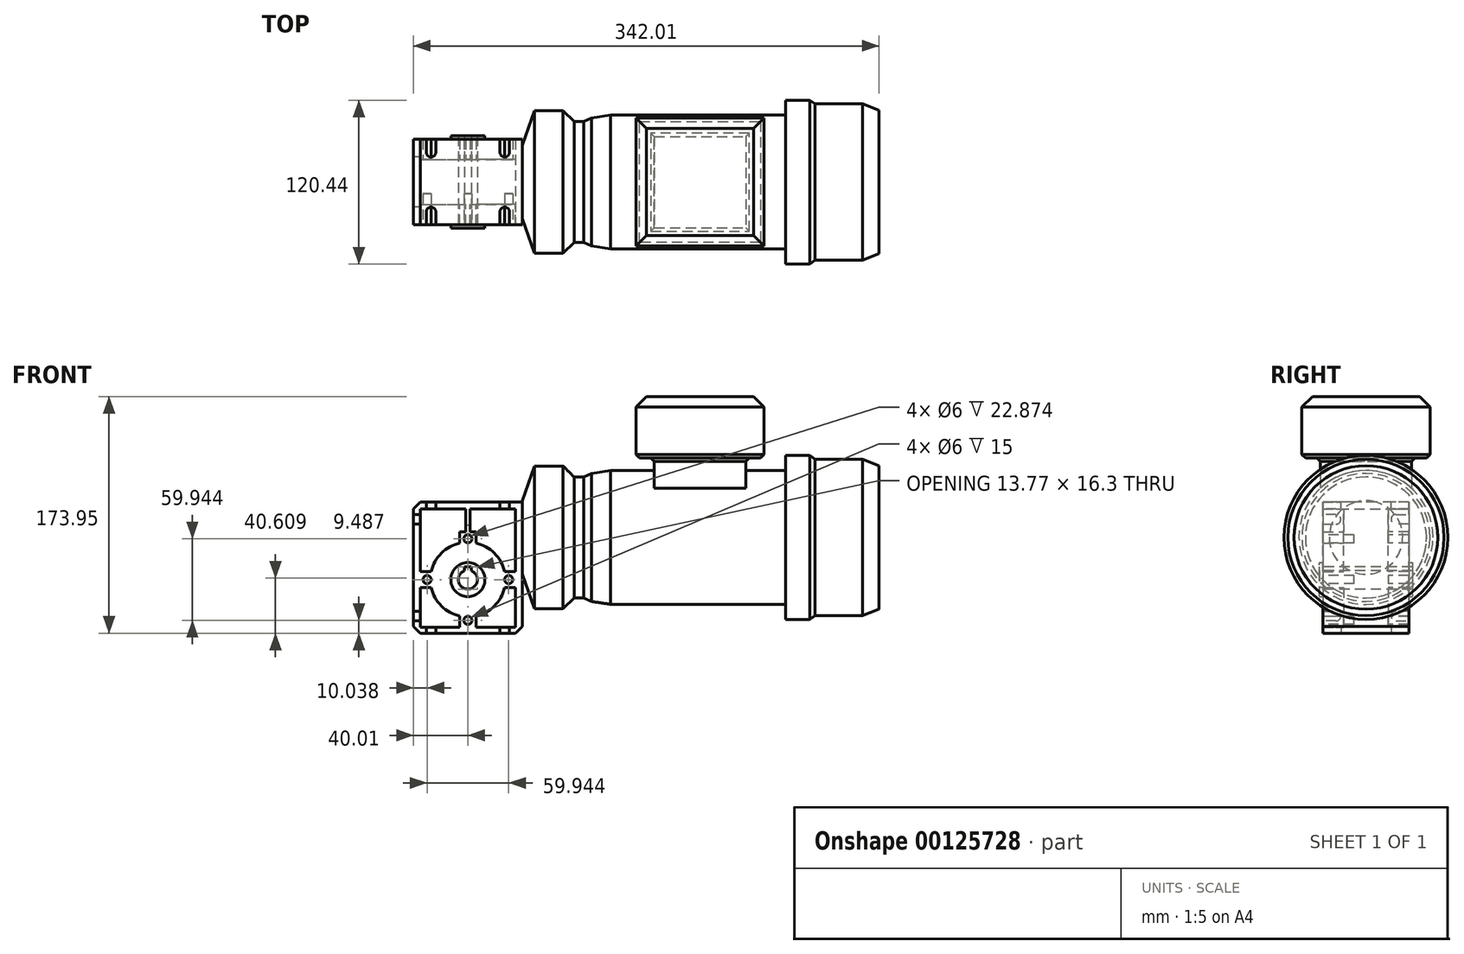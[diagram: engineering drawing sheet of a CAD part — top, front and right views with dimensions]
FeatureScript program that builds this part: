
annotation { "Feature Type Name" : "Feature", "Feature Type Description" : "" }
export const myFeature = defineFeature(function(context is Context, id is Id, definition is map)
    precondition{}
    {
        {
            var Q0;
            Q0=qCreatedBy(makeId("Top.planeOp"),FACE);
            var sketch = newSketch(context, id + "F0", { "sketchPlane" : qUnion([Q0])});
            skLineSegment(sketch, "E0.bottom", {"start": v(-40, 16.5) * mm, "end": v(40, 16.5) * mm});
            skLineSegment(sketch, "E0.top", {"start": v(-40, -16.5) * mm, "end": v(40, -16.5) * mm});
            skLineSegment(sketch, "E0.left", {"start": v(-40, 16.5) * mm, "end": v(-40, -16.5) * mm});
            skLineSegment(sketch, "E0.right", {"start": v(40, 16.5) * mm, "end": v(40, -16.5) * mm});
            skPoint(sketch, "E0.middle", {"position": v(0, 0) * mm});
            skSolve(sketch);
        }
        {
            var Q0;
            Q0=qSketchRegion(id+"F0",true);
            extrude(context, id + "F1", {"entities" : qUnion([Q0]), "depth" : 96.35 * mm, "symmetric" : true});
        }
        {
            var Q0;
            Q0=makeQuery(id+"F1.opExtrude","SWEPT_FACE",FACE,{"disambiguationData":[OSD([sQuery(id+"F0.wireOp",EDGE,"E0.top")])]});
            var sketch = newSketch(context, id + "F2", { "sketchPlane" : qUnion([Q0])});
            skArc(sketch, "E1", {"start": v(-2.5, -2.18) * mm, "mid": v(0, -15.72) * mm, "end": v(2.5, -2.18) * mm});
            skLineSegment(sketch, "E2", {"start": v(-2.5, -2.18) * mm, "end": v(-2.5, 0.58) * mm});
            skLineSegment(sketch, "E3", {"start": v(-2.5, 0.58) * mm, "end": v(2.5, 0.58) * mm});
            skLineSegment(sketch, "E4", {"start": v(2.5, 0.58) * mm, "end": v(2.5, -2.18) * mm});
            skPoint(sketch, "E5", {"position": v(0, -15.72) * mm});
            skSolve(sketch);
        }
        {
            var Q0;
            Q0=qSketchRegion(id+"F2",true);
            extrude(context, id + "F3", {"entities" : qUnion([Q0]), "operationType" : NewBodyOperationType.REMOVE, "endBound" : BoundingType.UP_TO_NEXT, "oppositeDirection" : true, "depth" : 25.4 * mm});
        }
        {
            var Q0;
            Q0=qCreatedBy(makeId("Front.planeOp"),FACE);
            var sketch = newSketch(context, id + "F4", { "sketchPlane" : qUnion([Q0])});
            skCircle(sketch, "E6", {"center": v(0, -8.72) * mm, "radius": 12.5 * mm});
            skArc(sketch, "E7.0", {"start": v(-2.5, -2.18) * mm, "mid": v(0, -15.72) * mm, "end": v(2.5, -2.18) * mm});
            skLineSegment(sketch, "E8.0", {"start": v(2.5, 0.58) * mm, "end": v(2.5, -2.18) * mm});
            skLineSegment(sketch, "E9.0", {"start": v(-2.5, 0.58) * mm, "end": v(2.5, 0.58) * mm});
            skLineSegment(sketch, "E10.0", {"start": v(-2.5, -2.18) * mm, "end": v(-2.5, 0.58) * mm});
            skSolve(sketch);
        }
        {
            var Q0;
            Q0=qSketchRegion(id+"F4",true);
            extrude(context, id + "F5", {"entities" : qUnion([Q0]), "operationType" : NewBodyOperationType.ADD, "depth" : 68.07 * mm, "symmetric" : true});
        }
        {
            var Q0;
            Q0=makeQuery(id+"F1.opExtrude","SWEPT_FACE",FACE,{"disambiguationData":[OSD([sQuery(id+"F0.wireOp",EDGE,"E0.top")])]});
            var sketch = newSketch(context, id + "F6", { "sketchPlane" : qUnion([Q0])});
            skCircle(sketch, "E11", {"center": v(0, 21.25) * mm, "radius": 3 * mm});
            skPoint(sketch, "E12", {"position": v(0, -8.72) * mm});
            skCircle(sketch, "E13.1.0", {"center": v(-29.97, -8.72) * mm, "radius": 3 * mm});
            skCircle(sketch, "E13.2.0", {"center": v(0, -38.7) * mm, "radius": 3 * mm});
            skCircle(sketch, "E13.3.0", {"center": v(29.97, -8.72) * mm, "radius": 3 * mm});
            skSolve(sketch);
        }
        {
            var Q0;
            Q0=qSketchRegion(id+"F6",true);
            extrude(context, id + "F7", {"entities" : qUnion([Q0]), "operationType" : NewBodyOperationType.REMOVE, "oppositeDirection" : true, "depth" : 7.87 * mm});
        }
        {
            var Q0;
            Q0=makeQuery(id+"F1.opExtrude","SWEPT_FACE",FACE,{"disambiguationData":[OSD([sQuery(id+"F0.wireOp",EDGE,"E0.top")])]});
            var sketch = newSketch(context, id + "F8", { "sketchPlane" : qUnion([Q0])});
            skLineSegment(sketch, "E14", {"start": v(-6, 18.12) * mm, "end": v(-6, 26.28) * mm});
            skLineSegment(sketch, "E15", {"start": v(-6, 26.28) * mm, "end": v(6, 26.28) * mm});
            skLineSegment(sketch, "E16", {"start": v(6, 26.28) * mm, "end": v(6, 18.12) * mm});
            skArc(sketch, "E17", {"start": v(-6, 18.12) * mm, "mid": v(-19.45, 10.72) * mm, "end": v(-26.84, -2.72) * mm});
            skArc(sketch, "E18", {"start": v(6, 18.12) * mm, "mid": v(0, 18.78) * mm, "end": v(-6, 18.12) * mm, "construction": true});
            skLineSegment(sketch, "E19", {"start": v(-6, -35.56) * mm, "end": v(-6, -35.56) * mm});
            skLineSegment(sketch, "E20", {"start": v(-6, -43.72) * mm, "end": v(6, -43.72) * mm});
            skLineSegment(sketch, "E21", {"start": v(6, -43.72) * mm, "end": v(6, -35.56) * mm});
            skLineSegment(sketch, "E22", {"start": v(-6, -35.56) * mm, "end": v(-6, -43.72) * mm});
            skArc(sketch, "E23", {"start": v(-6, -35.56) * mm, "mid": v(0, -36.22) * mm, "end": v(6, -35.56) * mm, "construction": true});
            skArc(sketch, "E24", {"start": v(6, -35.56) * mm, "mid": v(19.45, -28.17) * mm, "end": v(26.84, -14.72) * mm});
            skLineSegment(sketch, "E25", {"start": v(-35, -2.72) * mm, "end": v(-35, -14.72) * mm});
            skLineSegment(sketch, "E26", {"start": v(-35, -14.72) * mm, "end": v(-26.84, -14.72) * mm});
            skLineSegment(sketch, "E27", {"start": v(26.84, -2.72) * mm, "end": v(35, -2.72) * mm});
            skLineSegment(sketch, "E28", {"start": v(35, -2.72) * mm, "end": v(35, -14.72) * mm});
            skLineSegment(sketch, "E29", {"start": v(35, -14.72) * mm, "end": v(26.84, -14.72) * mm});
            skLineSegment(sketch, "E30", {"start": v(-35, -2.72) * mm, "end": v(-26.84, -2.72) * mm});
            skArc(sketch, "E31", {"start": v(-26.84, -2.72) * mm, "mid": v(-27.5, -8.72) * mm, "end": v(-26.84, -14.72) * mm, "construction": true});
            skArc(sketch, "E32", {"start": v(-26.84, -14.72) * mm, "mid": v(-19.45, -28.17) * mm, "end": v(-6, -35.56) * mm});
            skArc(sketch, "E33", {"start": v(26.84, -14.72) * mm, "mid": v(27.5, -8.72) * mm, "end": v(26.84, -2.72) * mm, "construction": true});
            skArc(sketch, "E34", {"start": v(26.84, -2.72) * mm, "mid": v(19.45, 10.72) * mm, "end": v(6, 18.12) * mm});
            skLineSegment(sketch, "E35", {"start": v(-35, -2.72) * mm, "end": v(-35, 43.17) * mm});
            skLineSegment(sketch, "E36", {"start": v(-35, 43.17) * mm, "end": v(-1.5, 43.17) * mm});
            skLineSegment(sketch, "E37", {"start": v(-1.5, 43.17) * mm, "end": v(-1.5, 26.28) * mm});
            skLineSegment(sketch, "E38", {"start": v(1.5, 26.28) * mm, "end": v(1.5, 43.17) * mm});
            skLineSegment(sketch, "E39", {"start": v(1.5, 43.17) * mm, "end": v(35, 43.17) * mm});
            skLineSegment(sketch, "E40", {"start": v(35, 43.17) * mm, "end": v(35, -2.72) * mm});
            skLineSegment(sketch, "E41", {"start": v(35, -14.72) * mm, "end": v(35, -43.72) * mm});
            skLineSegment(sketch, "E42", {"start": v(35, -43.72) * mm, "end": v(6, -43.72) * mm});
            skLineSegment(sketch, "E43", {"start": v(-35, -14.72) * mm, "end": v(-35, -43.72) * mm});
            skLineSegment(sketch, "E44", {"start": v(-35, -43.72) * mm, "end": v(-6, -43.72) * mm});
            skLineSegment(sketch, "E45", {"start": v(-35, 43.17) * mm, "end": v(-40, 43.17) * mm, "construction": true});
            skLineSegment(sketch, "E46", {"start": v(-35, 43.17) * mm, "end": v(-35, 48.17) * mm, "construction": true});
            skSolve(sketch);
        }
        {
            var Q0;
            Q0=makeQuery(id+"F8.imprint","IMPRINT",FACE,{"disambiguationData":[TD([[makeQuery(id+"F8.imprint","IMPRINT",EDGE,{"derivedFrom":sQuery(id+"F8.wireOp",EDGE,"E20")}),-1.0]])]});
            var Q1;
            {var subQ4=sQuery(id+"F8.wireOp",EDGE,"E14");Q1=makeQuery(id+"F8.imprint","IMPRINT",FACE,{"disambiguationData":[TD([[makeQuery(id+"F8.imprint","IMPRINT",EDGE,{"derivedFrom":subQ4}),-1.0]])]});}
            extrude(context, id + "F9", {"entities" : qUnion([Q0, Q1]), "depth" : 15 * mm});
        }
        {
            var Q0;
            Q0=makeQuery(id+"F9.opExtrude","SWEPT_BODY",BODY,{"disambiguationData":[OSD([sQuery(id+"F0.wireOp",EDGE,"E0.top"),sQuery(id+"F0.wireOp",EDGE,"E0.left"),sQuery(id+"F0.wireOp",EDGE,"E0.right"),sQuery(id+"F4.wireOp",EDGE,"E6"),sQuery(id+"F6.wireOp",EDGE,"E11"),sQuery(id+"F6.wireOp",EDGE,"E13.1.0"),sQuery(id+"F6.wireOp",EDGE,"E13.2.0"),sQuery(id+"F6.wireOp",EDGE,"E13.3.0"),sQuery(id+"F8.wireOp",EDGE,"E14"),sQuery(id+"F8.wireOp",EDGE,"E15"),sQuery(id+"F8.wireOp",EDGE,"E16"),sQuery(id+"F8.wireOp",EDGE,"E17"),sQuery(id+"F8.wireOp",EDGE,"E21"),sQuery(id+"F8.wireOp",EDGE,"E22"),sQuery(id+"F8.wireOp",EDGE,"E24"),sQuery(id+"F8.wireOp",EDGE,"E26"),sQuery(id+"F8.wireOp",EDGE,"E27"),sQuery(id+"F8.wireOp",EDGE,"E29"),sQuery(id+"F8.wireOp",EDGE,"E30"),sQuery(id+"F8.wireOp",EDGE,"E32"),sQuery(id+"F8.wireOp",EDGE,"E34"),sQuery(id+"F8.wireOp",EDGE,"E35"),sQuery(id+"F8.wireOp",EDGE,"E36"),sQuery(id+"F8.wireOp",EDGE,"E37"),sQuery(id+"F8.wireOp",EDGE,"E38"),sQuery(id+"F8.wireOp",EDGE,"E39"),sQuery(id+"F8.wireOp",EDGE,"E40"),sQuery(id+"F8.wireOp",EDGE,"E41"),sQuery(id+"F8.wireOp",EDGE,"E42"),sQuery(id+"F8.wireOp",EDGE,"E43"),sQuery(id+"F8.wireOp",EDGE,"E44")])]});
            var Q1;
            Q1=qCreatedBy(makeId("Front.planeOp"),FACE);
            mirror(context, id + "F10", {"operationType" : NewBodyOperationType.ADD, "entities" : qUnion([Q0]), "mirrorPlane" : qUnion([Q1])});
        }
        {
            var Q0;
            {var subQ0=sQuery(id+"F0.wireOp",EDGE,"E0.top");var subQ1=makeQuery(id+"F9.opExtrude","SWEPT_FACE",FACE,{"disambiguationData":[OSD([subQ0]),TDD([makeQuery(id+"F8.imprint","IMPRINT",EDGE,{"derivedFrom":makeQuery(id+"F1.opExtrude","CAP_EDGE",EDGE,{"disambiguationData":[OSD([subQ0])],"isStart":false})})])]});Q0=makeQuery(id+"F10.boolean.opBoolean","MERGE",FACE,{"derivedFrom":[makeQuery(id+"F1.opExtrude","CAP_FACE",FACE,{"disambiguationData":[OSD([sQuery(id+"F0.wireOp",EDGE,"E0.bottom"),subQ0,sQuery(id+"F0.wireOp",EDGE,"E0.left"),sQuery(id+"F0.wireOp",EDGE,"E0.right")])],"isStart":false}),subQ1,makeQuery(id+"F10.opPattern","COPY",FACE,{"derivedFrom":subQ1,"instanceName":"1"})]});}
            var sketch = newSketch(context, id + "F11", { "sketchPlane" : qUnion([Q0])});
            skLineSegment(sketch, "E47", {"start": v(-30.6, -31.5) * mm, "end": v(-30.6, -21.97) * mm});
            skLineSegment(sketch, "E48", {"start": v(-23.5, -31.5) * mm, "end": v(-23.5, -21.97) * mm});
            skArc(sketch, "E49", {"start": v(-30.6, -21.97) * mm, "mid": v(-27.05, -18.41) * mm, "end": v(-23.5, -21.97) * mm});
            skLineSegment(sketch, "E50", {"start": v(-30.6, -31.5) * mm, "end": v(-23.5, -31.5) * mm});
            skArc(sketch, "E51.MirrorCS", {"start": v(30.6, -21.97) * mm, "mid": v(27.05, -18.41) * mm, "end": v(23.5, -21.97) * mm});
            skLineSegment(sketch, "E52.MirrorCS", {"start": v(23.5, -31.5) * mm, "end": v(23.5, -21.97) * mm});
            skLineSegment(sketch, "E53.MirrorCS", {"start": v(30.6, -31.5) * mm, "end": v(30.6, -21.97) * mm});
            skLineSegment(sketch, "E54.MirrorCS", {"start": v(30.6, -31.5) * mm, "end": v(23.5, -31.5) * mm});
            skArc(sketch, "E55.MirrorCS", {"start": v(-30.6, 21.97) * mm, "mid": v(-27.05, 18.41) * mm, "end": v(-23.5, 21.97) * mm});
            skLineSegment(sketch, "E56.MirrorCS", {"start": v(-30.6, 31.5) * mm, "end": v(-30.6, 21.97) * mm});
            skLineSegment(sketch, "E57.MirrorCS", {"start": v(-23.5, 31.5) * mm, "end": v(-23.5, 21.97) * mm});
            skLineSegment(sketch, "E58.MirrorCS", {"start": v(-30.6, 31.5) * mm, "end": v(-23.5, 31.5) * mm});
            skLineSegment(sketch, "E59.MirrorCS", {"start": v(30.6, 31.5) * mm, "end": v(23.5, 31.5) * mm});
            skLineSegment(sketch, "E60.MirrorCS", {"start": v(23.5, 31.5) * mm, "end": v(23.5, 21.97) * mm});
            skArc(sketch, "E61.MirrorCS", {"start": v(30.6, 21.97) * mm, "mid": v(27.05, 18.41) * mm, "end": v(23.5, 21.97) * mm});
            skLineSegment(sketch, "E62.MirrorCS", {"start": v(30.6, 31.5) * mm, "end": v(30.6, 21.97) * mm});
            skSolve(sketch);
        }
        {
            var Q0;
            Q0=qSketchRegion(id+"F11",true);
            extrude(context, id + "F12", {"entities" : qUnion([Q0]), "operationType" : NewBodyOperationType.REMOVE, "endBound" : BoundingType.UP_TO_NEXT, "oppositeDirection" : true, "depth" : 114.3 * mm});
        }
        {
            var Q0;
            {var subQ0=sQuery(id+"F0.wireOp",EDGE,"E0.top");var subQ1=makeQuery(id+"F9.opExtrude","SWEPT_FACE",FACE,{"disambiguationData":[OSD([subQ0]),TDD([makeQuery(id+"F8.imprint","IMPRINT",EDGE,{"derivedFrom":makeQuery(id+"F1.opExtrude","CAP_EDGE",EDGE,{"disambiguationData":[OSD([subQ0])],"isStart":true})})])]});Q0=makeQuery(id+"F10.boolean.opBoolean","MERGE",FACE,{"derivedFrom":[makeQuery(id+"F1.opExtrude","CAP_FACE",FACE,{"disambiguationData":[OSD([sQuery(id+"F0.wireOp",EDGE,"E0.bottom"),subQ0,sQuery(id+"F0.wireOp",EDGE,"E0.left"),sQuery(id+"F0.wireOp",EDGE,"E0.right")])],"isStart":true}),subQ1,makeQuery(id+"F10.opPattern","COPY",FACE,{"derivedFrom":subQ1,"instanceName":"1"})]});}
            var sketch = newSketch(context, id + "F13", { "sketchPlane" : qUnion([Q0])});
            skLineSegment(sketch, "E63.0", {"start": v(-23.5, 21.97) * mm, "end": v(-23.5, 31.5) * mm});
            skArc(sketch, "E64.0", {"start": v(-23.5, 21.97) * mm, "mid": v(-27.05, 18.41) * mm, "end": v(-30.6, 21.97) * mm});
            skLineSegment(sketch, "E65.0", {"start": v(-30.6, 21.97) * mm, "end": v(-30.6, 31.5) * mm});
            skLineSegment(sketch, "E66.0", {"start": v(23.5, 21.97) * mm, "end": v(23.5, 31.5) * mm});
            skArc(sketch, "E67.0", {"start": v(23.5, 21.97) * mm, "mid": v(27.05, 18.41) * mm, "end": v(30.6, 21.97) * mm});
            skLineSegment(sketch, "E68.0", {"start": v(30.6, 21.97) * mm, "end": v(30.6, 31.5) * mm});
            skLineSegment(sketch, "E69", {"start": v(-30.6, 31.5) * mm, "end": v(-23.5, 31.5) * mm});
            skLineSegment(sketch, "E70", {"start": v(23.5, 31.5) * mm, "end": v(30.6, 31.5) * mm});
            skLineSegment(sketch, "E71.MirrorCS", {"start": v(23.5, -21.97) * mm, "end": v(23.5, -31.5) * mm});
            skArc(sketch, "E72.MirrorCS", {"start": v(23.5, -21.97) * mm, "mid": v(27.05, -18.41) * mm, "end": v(30.6, -21.97) * mm});
            skLineSegment(sketch, "E73.MirrorCS", {"start": v(30.6, -21.97) * mm, "end": v(30.6, -31.5) * mm});
            skLineSegment(sketch, "E74.MirrorCS", {"start": v(23.5, -31.5) * mm, "end": v(30.6, -31.5) * mm});
            skLineSegment(sketch, "E75.MirrorCS", {"start": v(-30.6, -31.5) * mm, "end": v(-23.5, -31.5) * mm});
            skLineSegment(sketch, "E76.MirrorCS", {"start": v(-30.6, -21.97) * mm, "end": v(-30.6, -31.5) * mm});
            skArc(sketch, "E77.MirrorCS", {"start": v(-23.5, -21.97) * mm, "mid": v(-27.05, -18.41) * mm, "end": v(-30.6, -21.97) * mm});
            skLineSegment(sketch, "E78.MirrorCS", {"start": v(-23.5, -21.97) * mm, "end": v(-23.5, -31.5) * mm});
            skSolve(sketch);
        }
        {
            var Q0;
            Q0=qSketchRegion(id+"F13",true);
            extrude(context, id + "F14", {"entities" : qUnion([Q0]), "operationType" : NewBodyOperationType.REMOVE, "endBound" : BoundingType.UP_TO_NEXT, "oppositeDirection" : true, "depth" : 25.4 * mm});
        }
        {
            var Q0;
            {var subQ0=sQuery(id+"F0.wireOp",EDGE,"E0.left");var subQ1=makeQuery(id+"F9.opExtrude","SWEPT_FACE",FACE,{"disambiguationData":[OSD([sQuery(id+"F0.wireOp",EDGE,"E0.top"),subQ0])]});Q0=makeQuery(id+"F10.boolean.opBoolean","MERGE",FACE,{"derivedFrom":[makeQuery(id+"F1.opExtrude","SWEPT_FACE",FACE,{"disambiguationData":[OSD([subQ0])]}),subQ1,makeQuery(id+"F10.opPattern","COPY",FACE,{"derivedFrom":subQ1,"instanceName":"1"})]});}
            var sketch = newSketch(context, id + "F15", { "sketchPlane" : qUnion([Q0])});
            skLineSegment(sketch, "E79", {"start": v(31.5, 39.12) * mm, "end": v(31.5, 32) * mm});
            skArc(sketch, "E80.MirrorCS", {"start": v(21.97, 39.12) * mm, "mid": v(18.42, 35.56) * mm, "end": v(21.97, 32) * mm});
            skLineSegment(sketch, "E81", {"start": v(21.97, 39.12) * mm, "end": v(31.5, 39.12) * mm});
            skLineSegment(sketch, "E82", {"start": v(31.5, 32) * mm, "end": v(21.97, 32) * mm});
            skArc(sketch, "E83.MirrorCS", {"start": v(-21.97, 39.12) * mm, "mid": v(-18.41, 35.56) * mm, "end": v(-21.97, 32) * mm});
            skLineSegment(sketch, "E84.MirrorCS", {"start": v(-21.97, 39.12) * mm, "end": v(-31.5, 39.12) * mm});
            skLineSegment(sketch, "E85.MirrorCS", {"start": v(-31.5, 32) * mm, "end": v(-21.97, 32) * mm});
            skLineSegment(sketch, "E86.MirrorCS", {"start": v(-31.5, 39.12) * mm, "end": v(-31.5, 32) * mm});
            skLineSegment(sketch, "E87.MirrorCS", {"start": v(-31.5, -39.12) * mm, "end": v(-31.5, -32) * mm});
            skLineSegment(sketch, "E88.MirrorCS", {"start": v(-31.5, -32) * mm, "end": v(-21.97, -32) * mm});
            skArc(sketch, "E89.MirrorCS", {"start": v(-21.97, -39.12) * mm, "mid": v(-18.41, -35.56) * mm, "end": v(-21.97, -32) * mm});
            skLineSegment(sketch, "E90.MirrorCS", {"start": v(-21.97, -39.12) * mm, "end": v(-31.5, -39.12) * mm});
            skArc(sketch, "E91.MirrorCS", {"start": v(21.97, -39.12) * mm, "mid": v(18.42, -35.56) * mm, "end": v(21.97, -32) * mm});
            skLineSegment(sketch, "E92.MirrorCS", {"start": v(31.5, -32) * mm, "end": v(21.97, -32) * mm});
            skLineSegment(sketch, "E93.MirrorCS", {"start": v(31.5, -39.12) * mm, "end": v(31.5, -32) * mm});
            skLineSegment(sketch, "E94.MirrorCS", {"start": v(21.97, -39.12) * mm, "end": v(31.5, -39.12) * mm});
            skSolve(sketch);
        }
        {
            var Q0;
            Q0=qSketchRegion(id+"F15",true);
            extrude(context, id + "F16", {"entities" : qUnion([Q0]), "operationType" : NewBodyOperationType.REMOVE, "endBound" : BoundingType.UP_TO_NEXT, "oppositeDirection" : true, "depth" : 25.4 * mm});
        }
        {
            var Q0;
            {var subQ0=sQuery(id+"F0.wireOp",EDGE,"E0.right");var subQ1=makeQuery(id+"F9.opExtrude","SWEPT_FACE",FACE,{"disambiguationData":[OSD([sQuery(id+"F0.wireOp",EDGE,"E0.top"),subQ0])]});Q0=makeQuery(id+"F10.boolean.opBoolean","MERGE",FACE,{"derivedFrom":[makeQuery(id+"F1.opExtrude","SWEPT_FACE",FACE,{"disambiguationData":[OSD([subQ0])]}),subQ1,makeQuery(id+"F10.opPattern","COPY",FACE,{"derivedFrom":subQ1,"instanceName":"1"})]});}
            var sketch = newSketch(context, id + "F17", { "sketchPlane" : qUnion([Q0])});
            skLineSegment(sketch, "E95.0", {"start": v(-8.62, -11.72) * mm, "end": v(-8.62, -5.72) * mm, "construction": true});
            skPoint(sketch, "E96", {"position": v(-8.62, -8.72) * mm});
            skCircle(sketch, "E97", {"center": v(0, 22.27) * mm, "radius": 27 * mm});
            skSolve(sketch);
        }
        {
            var Q0;
            {var subQ0=sQuery(id+"F0.wireOp",EDGE,"E0.left");var subQ1=makeQuery(id+"F9.opExtrude","SWEPT_FACE",FACE,{"disambiguationData":[OSD([sQuery(id+"F0.wireOp",EDGE,"E0.top"),subQ0])]});Q0=makeQuery(id+"F10.boolean.opBoolean","MERGE",FACE,{"derivedFrom":[makeQuery(id+"F1.opExtrude","SWEPT_FACE",FACE,{"disambiguationData":[OSD([subQ0])]}),subQ1,makeQuery(id+"F10.opPattern","COPY",FACE,{"derivedFrom":subQ1,"instanceName":"1"})]});}
            cPlane(context, id + "F18", {"entities" : qUnion([Q0]), "cplaneType" : CPlaneType.OFFSET, "offset" : 89 * mm, "oppositeDirection" : true, "width" : 152.4 * mm, "height" : 152.4 * mm});
        }
        {
            var Q0;
            Q0=qCreatedBy(id+"F18.planeOp",FACE);
            var sketch = newSketch(context, id + "F19", { "sketchPlane" : qUnion([Q0])});
            skCircle(sketch, "E98", {"center": v(0, 22.27) * mm, "radius": 52.45 * mm});
            skSolve(sketch);
        }
        {
            var Q1;
            Q1=qSketchRegion(id+"F17",true);
            var Q2;
            Q2=qSketchRegion(id+"F19",true);
            loft(context, id + "F20", {"operationType" : NewBodyOperationType.ADD, "sheetProfilesArray" : [{ "sheetProfileEntities" : qUnion([Q1]) }, { "sheetProfileEntities" : qUnion([Q2]) }]});
        }
        {
            var Q0;
            Q0=qSketchRegion(id+"F19",true);
            extrude(context, id + "F21", {"entities" : qUnion([Q0]), "operationType" : NewBodyOperationType.ADD, "oppositeDirection" : true, "depth" : 21 * mm});
        }
        {
            var Q0;
            Q0=makeQuery(id+"F21.opExtrude","CAP_FACE",FACE,{"disambiguationData":[OSD([sQuery(id+"F19.wireOp",EDGE,"E98")])],"isStart":false});
            cPlane(context, id + "F22", {"entities" : qUnion([Q0]), "cplaneType" : CPlaneType.OFFSET, "offset" : 8 * mm, "width" : 152.4 * mm, "height" : 152.4 * mm});
        }
        {
            var Q0;
            Q0=qCreatedBy(id+"F22.planeOp",FACE);
            var sketch = newSketch(context, id + "F23", { "sketchPlane" : qUnion([Q0])});
            skCircle(sketch, "E99", {"center": v(0, 22.27) * mm, "radius": 44.45 * mm});
            skSolve(sketch);
        }
        {
            var Q1;
            Q1=makeQuery(id+"F21.opExtrude","CAP_FACE",FACE,{"disambiguationData":[OSD([sQuery(id+"F19.wireOp",EDGE,"E98")])],"isStart":false});
            var Q2;
            Q2=makeQuery(id+"F23.imprint","IMPRINT",FACE,{"disambiguationData":[TD([[makeQuery(id+"F23.imprint","IMPRINT",EDGE,{"derivedFrom":sQuery(id+"F23.wireOp",EDGE,"E99")}),1.0]])]});
            loft(context, id + "F24", {"operationType" : NewBodyOperationType.ADD, "sheetProfilesArray" : [{ "sheetProfileEntities" : qUnion([Q1]) }, { "sheetProfileEntities" : qUnion([Q2]) }]});
        }
        {
            var Q0;
            Q0=qCreatedBy(makeId("Front.planeOp"),FACE);
            var sketch = newSketch(context, id + "F25", { "sketchPlane" : qUnion([Q0])});
            skLineSegment(sketch, "E100.0", {"start": v(78, 66.72) * mm, "end": v(78, -22.18) * mm, "construction": true});
            skPoint(sketch, "E101", {"position": v(78, 22.27) * mm});
            skLineSegment(sketch, "E102", {"start": v(78, 66.72) * mm, "end": v(84.97, 66.72) * mm});
            skLineSegment(sketch, "E103", {"start": v(84.97, 66.72) * mm, "end": v(90.65, 69.3) * mm});
            skLineSegment(sketch, "E104", {"start": v(90.65, 69.3) * mm, "end": v(104.92, 71.49) * mm});
            skLineSegment(sketch, "E105", {"start": v(104.92, 71.49) * mm, "end": v(233.25, 71.49) * mm});
            skLineSegment(sketch, "E106", {"start": v(233.25, 71.49) * mm, "end": v(233.25, 82.49) * mm});
            skLineSegment(sketch, "E107", {"start": v(233.25, 82.49) * mm, "end": v(251.25, 82.49) * mm});
            skLineSegment(sketch, "E108", {"start": v(251.25, 82.49) * mm, "end": v(255, 79.65) * mm});
            skLineSegment(sketch, "E109", {"start": v(255, 79.65) * mm, "end": v(290, 79.65) * mm});
            skLineSegment(sketch, "E110", {"start": v(290, 79.65) * mm, "end": v(302, 75.05) * mm});
            skLineSegment(sketch, "E111", {"start": v(302, 75.05) * mm, "end": v(302, 22.27) * mm});
            skLineSegment(sketch, "E112", {"start": v(302, 22.27) * mm, "end": v(78, 22.27) * mm});
            skLineSegment(sketch, "E113", {"start": v(78, 66.72) * mm, "end": v(78, 22.27) * mm});
            skSolve(sketch);
        }
        {
            var Q0;
            Q0=makeQuery(id+"F25.imprint","IMPRINT",FACE,{"disambiguationData":[TD([[makeQuery(id+"F25.imprint","IMPRINT",EDGE,{"derivedFrom":sQuery(id+"F25.wireOp",EDGE,"E102")}),-1.0]])]});
            var Q1;
            Q1=sQuery(id+"F25.wireOp",EDGE,"E112");
            revolve(context, id + "F26", {"operationType" : NewBodyOperationType.ADD, "entities" : qUnion([Q0]), "axis" : qUnion([Q1]), "revolveType" : RevolveType.FULL});
        }
        {
            var Q0;
            Q0=qCreatedBy(makeId("Top.planeOp"),FACE);
            var sketch = newSketch(context, id + "F27", { "sketchPlane" : qUnion([Q0])});
            skLineSegment(sketch, "E114.bottom", {"start": v(204, 33.5) * mm, "end": v(137, 33.5) * mm});
            skLineSegment(sketch, "E114.top", {"start": v(204, -33.5) * mm, "end": v(137, -33.5) * mm});
            skLineSegment(sketch, "E114.left", {"start": v(204, 33.5) * mm, "end": v(204, -33.5) * mm});
            skLineSegment(sketch, "E114.right", {"start": v(137, 33.5) * mm, "end": v(137, -33.5) * mm});
            skPoint(sketch, "E114.middle", {"position": v(170.5, 0) * mm});
            skSolve(sketch);
        }
        {
            var Q0;
            Q0=qSketchRegion(id+"F27",true);
            extrude(context, id + "F28", {"entities" : qUnion([Q0]), "operationType" : NewBodyOperationType.ADD, "depth" : 80.77 * mm});
        }
        {
            var Q0;
            Q0=makeQuery(id+"F28.opExtrude","CAP_FACE",FACE,{"disambiguationData":[OSD([sQuery(id+"F27.wireOp",EDGE,"E114.bottom"),sQuery(id+"F27.wireOp",EDGE,"E114.top"),sQuery(id+"F27.wireOp",EDGE,"E114.left"),sQuery(id+"F27.wireOp",EDGE,"E114.right")])],"isStart":false});
            var sketch = newSketch(context, id + "F29", { "sketchPlane" : qUnion([Q0])});
            skLineSegment(sketch, "E115.bottom", {"start": v(123.5, 47) * mm, "end": v(217.5, 47) * mm});
            skLineSegment(sketch, "E115.top", {"start": v(123.5, -47) * mm, "end": v(217.5, -47) * mm});
            skLineSegment(sketch, "E115.left", {"start": v(123.5, 47) * mm, "end": v(123.5, -47) * mm});
            skLineSegment(sketch, "E115.right", {"start": v(217.5, 47) * mm, "end": v(217.5, -47) * mm});
            skPoint(sketch, "E115.middle", {"position": v(170.5, 0) * mm});
            skPoint(sketch, "E116", {"position": v(170.5, 33.5) * mm});
            skPoint(sketch, "E117", {"position": v(170.5, 47) * mm});
            skSolve(sketch);
        }
        {
            var Q0;
            Q0=qSketchRegion(id+"F29",true);
            extrude(context, id + "F30", {"entities" : qUnion([Q0]), "operationType" : NewBodyOperationType.ADD, "depth" : 45 * mm});
        }
        {
            var Q0;
            Q0=makeQuery(id+"F30.opExtrude","CAP_FACE",FACE,{"disambiguationData":[OSD([sQuery(id+"F29.wireOp",EDGE,"E115.bottom"),sQuery(id+"F29.wireOp",EDGE,"E115.top"),sQuery(id+"F29.wireOp",EDGE,"E115.left"),sQuery(id+"F29.wireOp",EDGE,"E115.right")])],"isStart":false});
            chamfer(context, id + "F31", {"entities" : qUnion([Q0]), "width" : 7.62 * mm, "tangentPropagation" : true});
        }
        {
            var Q0;
            Q0=makeQuery(id+"F30.opExtrude","CAP_FACE",FACE,{"disambiguationData":[OSD([sQuery(id+"F29.wireOp",EDGE,"E115.bottom"),sQuery(id+"F29.wireOp",EDGE,"E115.top"),sQuery(id+"F29.wireOp",EDGE,"E115.left"),sQuery(id+"F29.wireOp",EDGE,"E115.right")])],"isStart":true});
            chamfer(context, id + "F32", {"entities" : qUnion([Q0]), "width" : 2.54 * mm, "tangentPropagation" : true});
        }
        {
            var Q0;
            {var subQ0=sQuery(id+"F0.wireOp",EDGE,"E0.top");var subQ1=sQuery(id+"F0.wireOp",EDGE,"E0.left");var subQ2=makeQuery(id+"F9.opExtrude","SWEPT_EDGE",EDGE,{"disambiguationData":[OSD([subQ0,subQ1]),TDD([makeQuery(id+"F8.imprint","INTERSECT",VERTEX,{"derivedFrom":[makeQuery(id+"F1.opExtrude","SWEPT_EDGE",EDGE,{"disambiguationData":[OSD([subQ0,subQ1])]}),makeQuery(id+"F1.opExtrude","CAP_EDGE",EDGE,{"disambiguationData":[OSD([subQ0])],"isStart":false})]})])]});Q0=makeQuery(id+"F10.boolean.opBoolean","MERGE",EDGE,{"derivedFrom":[makeQuery(id+"F1.opExtrude","CAP_EDGE",EDGE,{"disambiguationData":[OSD([subQ1])],"isStart":false}),subQ2,makeQuery(id+"F10.opPattern","COPY",EDGE,{"derivedFrom":subQ2,"instanceName":"1"})]});}
            var Q1;
            {var subQ0=sQuery(id+"F0.wireOp",EDGE,"E0.top");var subQ1=sQuery(id+"F0.wireOp",EDGE,"E0.left");var subQ2=makeQuery(id+"F9.opExtrude","SWEPT_EDGE",EDGE,{"disambiguationData":[OSD([subQ0,subQ1]),TDD([makeQuery(id+"F8.imprint","INTERSECT",VERTEX,{"derivedFrom":[makeQuery(id+"F1.opExtrude","SWEPT_EDGE",EDGE,{"disambiguationData":[OSD([subQ0,subQ1])]}),makeQuery(id+"F1.opExtrude","CAP_EDGE",EDGE,{"disambiguationData":[OSD([subQ0])],"isStart":true})]})])]});Q1=makeQuery(id+"F10.boolean.opBoolean","MERGE",EDGE,{"derivedFrom":[makeQuery(id+"F1.opExtrude","CAP_EDGE",EDGE,{"disambiguationData":[OSD([subQ1])],"isStart":true}),subQ2,makeQuery(id+"F10.opPattern","COPY",EDGE,{"derivedFrom":subQ2,"instanceName":"1"})]});}
            var Q2;
            {var subQ0=sQuery(id+"F0.wireOp",EDGE,"E0.top");var subQ1=sQuery(id+"F0.wireOp",EDGE,"E0.right");var subQ2=makeQuery(id+"F9.opExtrude","SWEPT_EDGE",EDGE,{"disambiguationData":[OSD([subQ0,subQ1]),TDD([makeQuery(id+"F8.imprint","INTERSECT",VERTEX,{"derivedFrom":[makeQuery(id+"F1.opExtrude","SWEPT_EDGE",EDGE,{"disambiguationData":[OSD([subQ0,subQ1])]}),makeQuery(id+"F1.opExtrude","CAP_EDGE",EDGE,{"disambiguationData":[OSD([subQ0])],"isStart":true})]})])]});Q2=makeQuery(id+"F10.boolean.opBoolean","MERGE",EDGE,{"derivedFrom":[makeQuery(id+"F1.opExtrude","CAP_EDGE",EDGE,{"disambiguationData":[OSD([subQ1])],"isStart":true}),subQ2,makeQuery(id+"F10.opPattern","COPY",EDGE,{"derivedFrom":subQ2,"instanceName":"1"})]});}
            chamfer(context, id + "F33", {"entities" : qUnion([Q0, Q1, Q2]), "width" : 5.08 * mm, "tangentPropagation" : true});
        }
    });
